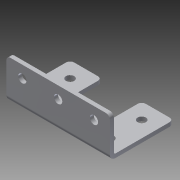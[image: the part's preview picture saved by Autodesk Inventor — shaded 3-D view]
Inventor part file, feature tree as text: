
AUTODESK INVENTOR PART (.ipt)
format: ipt  version: 2013 (Build 170138000, 138)  size: 163,840 bytes
history: native  units: in
note: dims shown in document units (in); Inventor stores cm internally (conversion verified against a paired STEP export)
features: sheet_metal_op x4, sketch x3, other x3, chamfer x1
ambient origin geometry x8: Origin, YZ Plane, XZ Plane, XY Plane, X Axis, Y Axis, Z Axis, Center Point
bodies: Solid1 (feature_tree)
feature tree (11):
  sheet_metal_op  "Face1"
  sheet_metal_op  "Flange1"
  chamfer  "Corner Round1"
  sketch  "Sketch1"  dims[d0=3.25in]
  other  "Plate1"
  sketch  "Sketch2"  dims[d2=0.5in]
  other  "Plate2"
  sheet_metal_op  "Bend1"
  sheet_metal_op  "Corner1"
  sketch  "Sketch3"  dims[d3=0.5in d4=0.26in d5=0.75in d6=0.75in d7=0.5in d8=1.0in d9=1.0in d10=0.5in d11=0.5in d12=1.0in d13=0.125in d14=0.125in d15=0.0625in d16=0.25in d17=0.125in d18=1.25in d19=90.0deg d20=0.05in d21=0.5in d22=0.125in d23=0.125in d24=0.26in d26=0.5in d27=0.875in d28=0.125in d29=0.0in d30=0.125in]
  other  "Cut1"
